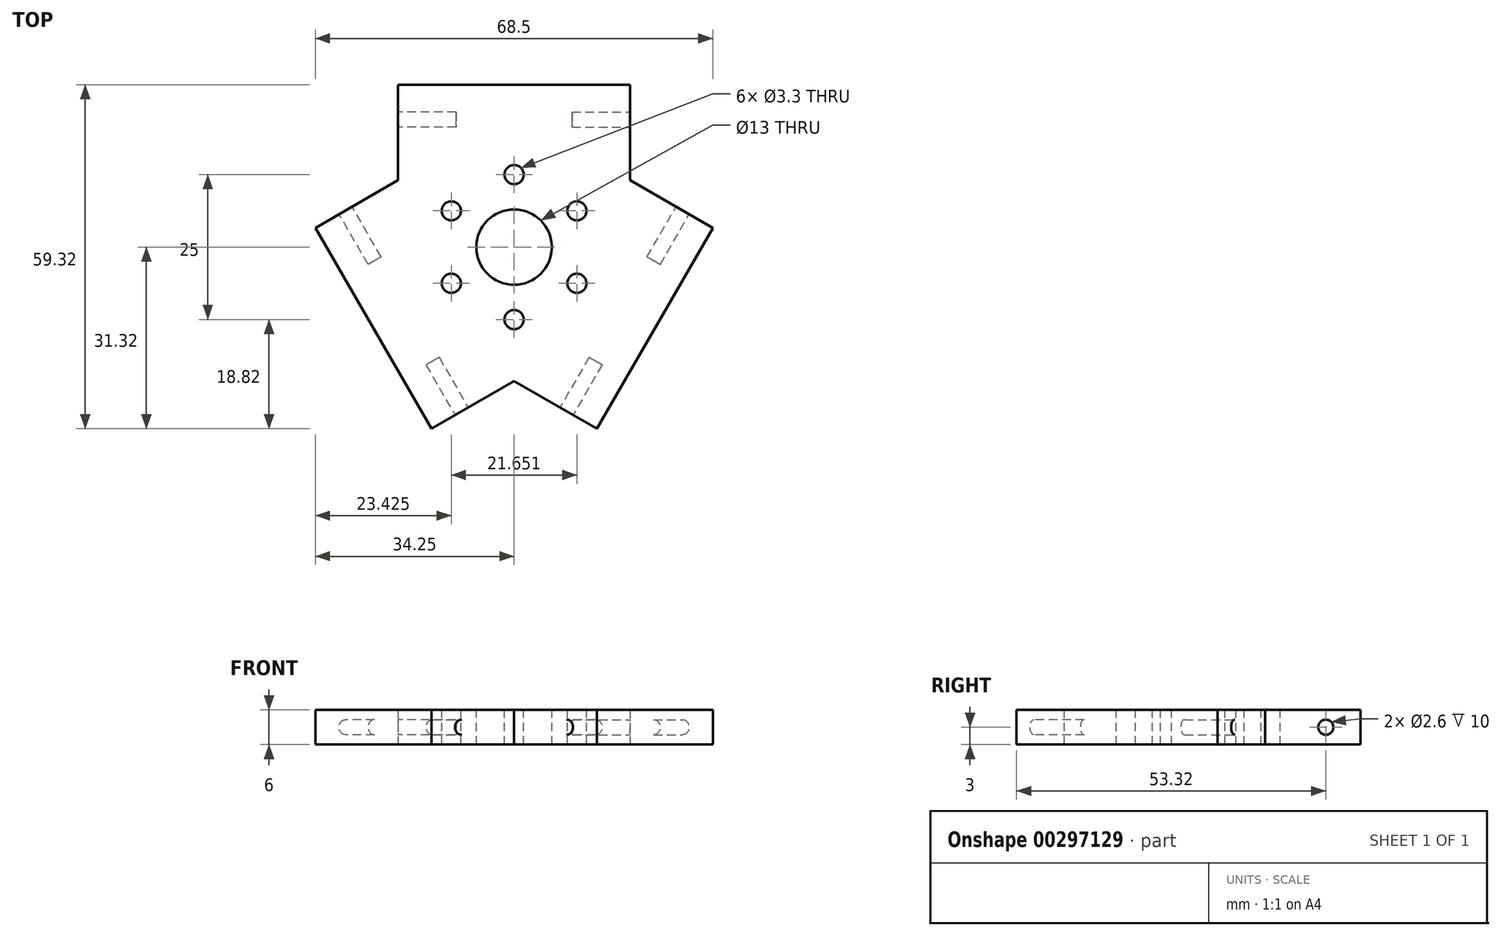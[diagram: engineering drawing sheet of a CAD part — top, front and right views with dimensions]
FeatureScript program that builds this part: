
annotation { "Feature Type Name" : "Feature", "Feature Type Description" : "" }
export const myFeature = defineFeature(function(context is Context, id is Id, definition is map)
    precondition{}
    {
        {
            var Q0;
            Q0=qCreatedBy(makeId("Top.planeOp"),FACE);
            var sketch = newSketch(context, id + "F0", { "sketchPlane" : qUnion([Q0])});
            skLineSegment(sketch, "E0", {"start": v(20, 28) * mm, "end": v(20, -11.09) * mm, "construction": true});
            skLineSegment(sketch, "E1", {"start": v(-20, -12.51) * mm, "end": v(-20, 28) * mm, "construction": true});
            skLineSegment(sketch, "E2", {"start": v(-33.34, 22) * mm, "end": v(37, 22) * mm, "construction": true});
            skLineSegment(sketch, "E3.bottom", {"start": v(-20, 28) * mm, "end": v(20, 28) * mm});
            skLineSegment(sketch, "E3.top", {"start": v(-20, 0) * mm, "end": v(20, 0) * mm});
            skLineSegment(sketch, "E3.left", {"start": v(-20, 28) * mm, "end": v(-20, 0) * mm});
            skLineSegment(sketch, "E3.right", {"start": v(20, 28) * mm, "end": v(20, 0) * mm});
            skSolve(sketch);
        }
        {
            var Q0;
            Q0 = qSketchRegion(id + "F0", true);
            extrude(context, id + "F1", {"entities" : qUnion([Q0]), "depth" : 6 * mm});
        }
        {
            var Q0;
            Q0=makeQuery(id+"F1.opExtrude","SWEPT_FACE",FACE,{"disambiguationData":[OSD([sQuery(id+"F0.wireOp",EDGE,"E3.left")])]});
            var sketch = newSketch(context, id + "F2", { "sketchPlane" : qUnion([Q0])});
            skLineSegment(sketch, "E4", {"start": v(-22, 0) * mm, "end": v(-22, 7.65) * mm, "construction": true});
            skCircle(sketch, "E5", {"center": v(-22, 3) * mm, "radius": 1.3 * mm});
            skSolve(sketch);
        }
        {
            var Q0;
            Q0 = qSketchRegion(id + "F2", true);
            extrude(context, id + "F3", {"entities" : qUnion([Q0]), "operationType" : NewBodyOperationType.REMOVE, "oppositeDirection" : true, "depth" : 10 * mm});
        }
        {
            var Q0;
            Q0=makeQuery(id+"F1.opExtrude","SWEPT_BODY",BODY,{"disambiguationData":[OSD([sQuery(id+"F0.wireOp",EDGE,"E3.bottom"),sQuery(id+"F0.wireOp",EDGE,"E3.top"),sQuery(id+"F0.wireOp",EDGE,"E3.left"),sQuery(id+"F0.wireOp",EDGE,"E3.right")])]});
            var Q1;
            Q1=qCreatedBy(makeId("Right.planeOp"),FACE);
            mirror(context, id + "F4", {"operationType" : NewBodyOperationType.INTERSECT, "entities" : qUnion([Q0]), "mirrorPlane" : qUnion([Q1])});
        }
        {
            var Q0;
            Q0=qCreatedBy(makeId("Front.planeOp"),FACE);
            var sketch = newSketch(context, id + "F5", { "sketchPlane" : qUnion([Q0])});
            skLineSegment(sketch, "E6", {"start": v(0, 0) * mm, "end": v(0, 16.8) * mm, "construction": true});
            skSolve(sketch);
        }
        {
            var Q0;
            Q0=makeQuery(id+"F1.opExtrude","SWEPT_BODY",BODY,{"disambiguationData":[OSD([sQuery(id+"F0.wireOp",EDGE,"E3.bottom"),sQuery(id+"F0.wireOp",EDGE,"E3.top"),sQuery(id+"F0.wireOp",EDGE,"E3.left"),sQuery(id+"F0.wireOp",EDGE,"E3.right")])]});
            var Q1;
            Q1=sQuery(id+"F5.wireOp",EDGE,"E6");
            circularPattern(context, id + "F6", {"operationType" : NewBodyOperationType.ADD, "entities" : qUnion([Q0]), "axis" : qUnion([Q1]), "angle" : 360 * degree, "instanceCount" : 3, "equalSpace" : true});
        }
        {
            var Q0;
            {var subQ0=makeQuery(id+"F1.opExtrude","CAP_FACE",FACE,{"disambiguationData":[OSD([sQuery(id+"F0.wireOp",EDGE,"E3.bottom"),sQuery(id+"F0.wireOp",EDGE,"E3.top"),sQuery(id+"F0.wireOp",EDGE,"E3.left"),sQuery(id+"F0.wireOp",EDGE,"E3.right")])],"isStart":false});Q0=makeQuery(id+"F6.boolean.opBoolean","MERGE",FACE,{"derivedFrom":[subQ0,makeQuery(id+"F6.opPattern","COPY",FACE,{"derivedFrom":subQ0,"instanceName":"1"}),makeQuery(id+"F6.opPattern","COPY",FACE,{"derivedFrom":subQ0,"instanceName":"2"})]});}
            var sketch = newSketch(context, id + "F7", { "sketchPlane" : qUnion([Q0])});
            skCircle(sketch, "E7", {"center": v(0, 0) * mm, "radius": 6.5 * mm});
            skCircle(sketch, "E8", {"center": v(0, -12.5) * mm, "radius": 1.65 * mm});
            skCircle(sketch, "E9.1.0", {"center": v(10.83, -6.25) * mm, "radius": 1.65 * mm});
            skCircle(sketch, "E9.2.0", {"center": v(10.83, 6.25) * mm, "radius": 1.65 * mm});
            skCircle(sketch, "E9.3.0", {"center": v(0, 12.5) * mm, "radius": 1.65 * mm});
            skCircle(sketch, "E9.4.0", {"center": v(-10.83, 6.25) * mm, "radius": 1.65 * mm});
            skCircle(sketch, "E9.5.0", {"center": v(-10.83, -6.25) * mm, "radius": 1.65 * mm});
            skSolve(sketch);
        }
        {
            var Q0;
            Q0=makeQuery(id+"F7.imprint","IMPRINT",FACE,{"disambiguationData":[TD([[makeQuery(id+"F7.imprint","IMPRINT",EDGE,{"derivedFrom":sQuery(id+"F7.wireOp",EDGE,"E7")}),1.0]])]});
            var Q1;
            Q1=makeQuery(id+"F7.imprint","IMPRINT",FACE,{"disambiguationData":[TD([[makeQuery(id+"F7.imprint","IMPRINT",EDGE,{"derivedFrom":sQuery(id+"F7.wireOp",EDGE,"E9.3.0")}),1.0]])]});
            var Q2;
            Q2=makeQuery(id+"F7.imprint","IMPRINT",FACE,{"disambiguationData":[TD([[makeQuery(id+"F7.imprint","IMPRINT",EDGE,{"derivedFrom":sQuery(id+"F7.wireOp",EDGE,"E9.2.0")}),1.0]])]});
            var Q3;
            Q3=makeQuery(id+"F7.imprint","IMPRINT",FACE,{"disambiguationData":[TD([[makeQuery(id+"F7.imprint","IMPRINT",EDGE,{"derivedFrom":sQuery(id+"F7.wireOp",EDGE,"E9.1.0")}),1.0]])]});
            var Q4;
            Q4=makeQuery(id+"F7.imprint","IMPRINT",FACE,{"disambiguationData":[TD([[makeQuery(id+"F7.imprint","IMPRINT",EDGE,{"derivedFrom":sQuery(id+"F7.wireOp",EDGE,"E8")}),1.0]])]});
            var Q5;
            Q5=makeQuery(id+"F7.imprint","IMPRINT",FACE,{"disambiguationData":[TD([[makeQuery(id+"F7.imprint","IMPRINT",EDGE,{"derivedFrom":sQuery(id+"F7.wireOp",EDGE,"E9.4.0")}),1.0]])]});
            var Q6;
            Q6=makeQuery(id+"F7.imprint","IMPRINT",FACE,{"disambiguationData":[TD([[makeQuery(id+"F7.imprint","IMPRINT",EDGE,{"derivedFrom":sQuery(id+"F7.wireOp",EDGE,"E9.5.0")}),1.0]])]});
            extrude(context, id + "F8", {"entities" : qUnion([Q0, Q1, Q2, Q3, Q4, Q5, Q6]), "operationType" : NewBodyOperationType.REMOVE, "endBound" : BoundingType.THROUGH_ALL, "oppositeDirection" : true, "depth" : 25 * mm});
        }
    });
